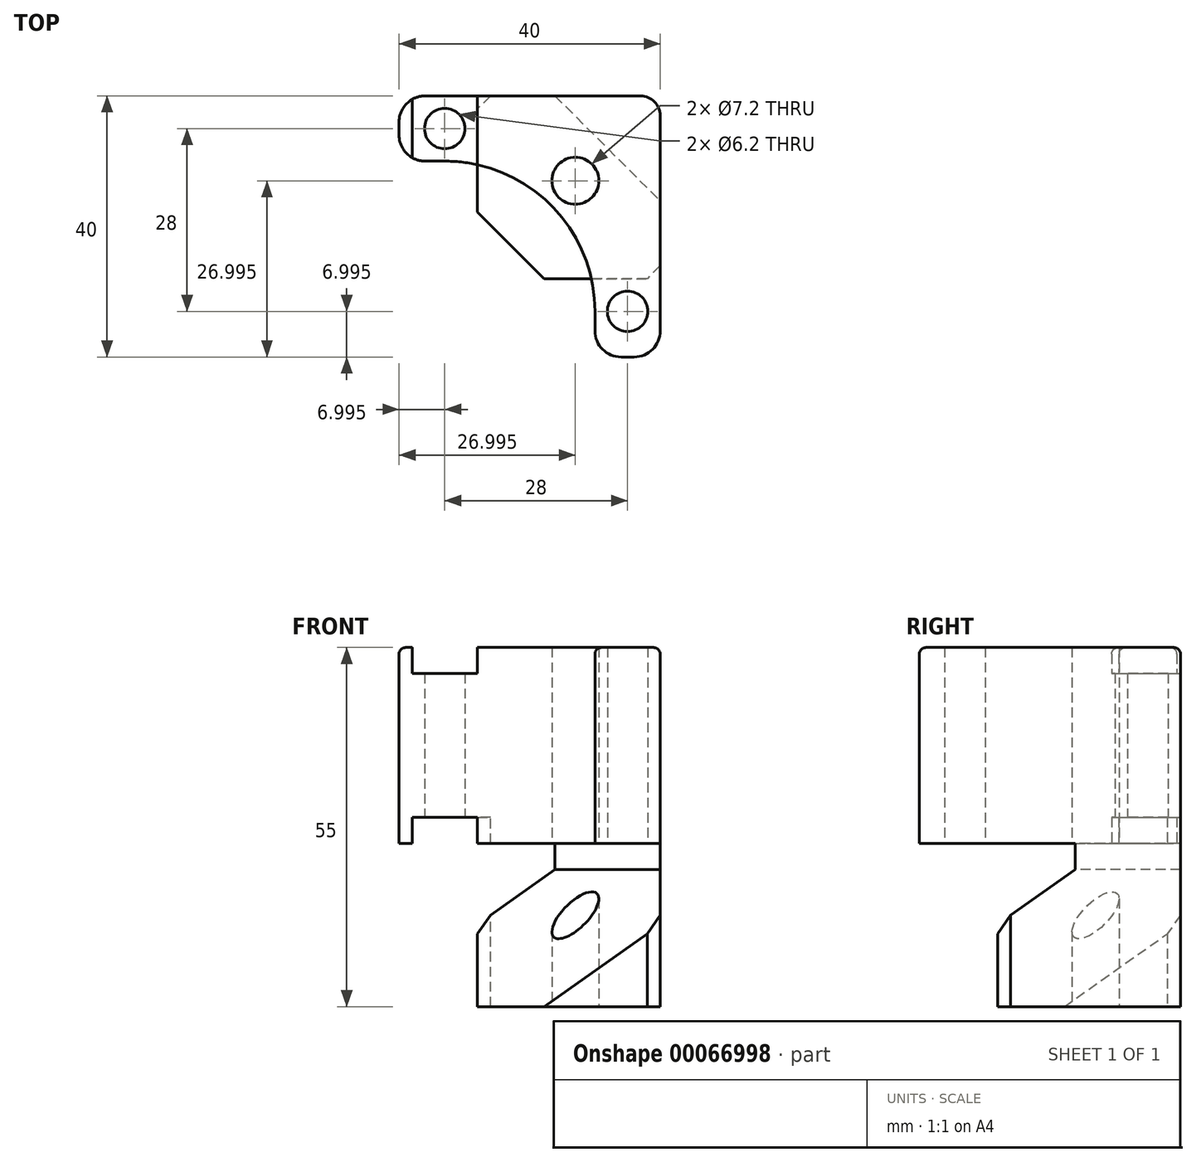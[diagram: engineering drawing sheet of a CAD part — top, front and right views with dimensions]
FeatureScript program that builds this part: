
annotation { "Feature Type Name" : "Feature", "Feature Type Description" : "" }
export const myFeature = defineFeature(function(context is Context, id is Id, definition is map)
    precondition{}
    {
        {
            var Q0;
            Q0=qCreatedBy(makeId("Top.planeOp"),FACE);
            var sketch = newSketch(context, id + "F0", { "sketchPlane" : qUnion([Q0])});
            skCircle(sketch, "E0", {"center": v(0, 0) * mm, "radius": 27.5 * mm, "construction": true});
            skLineSegment(sketch, "E1", {"start": v(-16.55, 19.45) * mm, "end": v(16.45, 19.45) * mm});
            skLineSegment(sketch, "E2", {"start": v(15.45, -20.55) * mm, "end": v(13.45, -20.55) * mm});
            skLineSegment(sketch, "E3", {"start": v(9.45, -16.55) * mm, "end": v(9.45, -13.55) * mm});
            skLineSegment(sketch, "E4", {"start": v(-13.55, 9.45) * mm, "end": v(-16.55, 9.45) * mm});
            skLineSegment(sketch, "E5", {"start": v(-20.55, 13.45) * mm, "end": v(-20.55, 15.45) * mm});
            skLineSegment(sketch, "E6", {"start": v(19.45, 16.45) * mm, "end": v(19.45, -16.55) * mm});
            skPoint(sketch, "E7.visualSharp", {"position": v(19.45, 19.45) * mm});
            skArc(sketch, "E7.filletArc", {"start": v(19.45, 16.45) * mm, "mid": v(18.57, 18.57) * mm, "end": v(16.45, 19.45) * mm});
            skPoint(sketch, "E8.visualSharp", {"position": v(-20.55, 19.45) * mm});
            skArc(sketch, "E8.filletArc", {"start": v(-16.55, 19.45) * mm, "mid": v(-19.38, 18.27) * mm, "end": v(-20.55, 15.45) * mm});
            skPoint(sketch, "E9.visualSharp", {"position": v(-20.55, 9.45) * mm});
            skArc(sketch, "E9.filletArc", {"start": v(-20.55, 13.45) * mm, "mid": v(-19.38, 10.62) * mm, "end": v(-16.55, 9.45) * mm});
            skPoint(sketch, "E10.visualSharp", {"position": v(9.45, -20.55) * mm});
            skArc(sketch, "E10.filletArc", {"start": v(9.45, -16.55) * mm, "mid": v(10.62, -19.38) * mm, "end": v(13.45, -20.55) * mm});
            skPoint(sketch, "E11.visualSharp", {"position": v(19.45, -20.55) * mm});
            skArc(sketch, "E11.filletArc", {"start": v(15.45, -20.55) * mm, "mid": v(18.27, -19.38) * mm, "end": v(19.45, -16.55) * mm});
            skLineSegment(sketch, "E12", {"start": v(0, 0) * mm, "end": v(19.45, 19.45) * mm, "construction": true});
            skPoint(sketch, "E13.visualSharp", {"position": v(9.45, 9.45) * mm});
            skArc(sketch, "E13.filletArc", {"start": v(9.45, -13.55) * mm, "mid": v(2.7, 2.7) * mm, "end": v(-13.55, 9.45) * mm});
            skCircle(sketch, "E14", {"center": v(6.45, 6.45) * mm, "radius": 3.6 * mm});
            skCircle(sketch, "E15", {"center": v(-13.55, 14.45) * mm, "radius": 3.1 * mm});
            skCircle(sketch, "E16", {"center": v(14.45, -13.55) * mm, "radius": 3.1 * mm});
            skLineSegment(sketch, "E17", {"start": v(-13.55, 14.45) * mm, "end": v(14.45, -13.55) * mm, "construction": true});
            skSolve(sketch);
        }
        {
            var Q0;
            Q0 = qSketchRegion(id + "F0", true);
            extrude(context, id + "F1", {"entities" : qUnion([Q0]), "depth" : 30 * mm});
        }
        {
            var Q0;
            Q0=makeQuery(id+"F1.opExtrude","SWEPT_FACE",FACE,{"disambiguationData":[OSD([sQuery(id+"F0.wireOp",EDGE,"E1")])]});
            var sketch = newSketch(context, id + "F2", { "sketchPlane" : qUnion([Q0])});
            skLineSegment(sketch, "E18.bottom", {"start": v(8.55, 30) * mm, "end": v(18.55, 30) * mm});
            skLineSegment(sketch, "E18.top", {"start": v(8.55, 26) * mm, "end": v(18.55, 26) * mm});
            skLineSegment(sketch, "E18.left", {"start": v(8.55, 30) * mm, "end": v(8.55, 26) * mm});
            skLineSegment(sketch, "E18.right", {"start": v(18.55, 30) * mm, "end": v(18.55, 26) * mm});
            skLineSegment(sketch, "E19.bottom", {"start": v(8.55, 0) * mm, "end": v(18.55, 0) * mm});
            skLineSegment(sketch, "E19.top", {"start": v(8.55, 4) * mm, "end": v(18.55, 4) * mm});
            skLineSegment(sketch, "E19.left", {"start": v(8.55, 0) * mm, "end": v(8.55, 4) * mm});
            skLineSegment(sketch, "E19.right", {"start": v(18.55, 0) * mm, "end": v(18.55, 4) * mm});
            skSolve(sketch);
        }
        {
            var Q0;
            Q0 = qSketchRegion(id + "F2", true);
            extrude(context, id + "F3", {"entities" : qUnion([Q0]), "operationType" : NewBodyOperationType.REMOVE, "endBound" : BoundingType.THROUGH_ALL, "oppositeDirection" : true, "depth" : 25 * mm});
        }
        {
            var Q0;
            Q0=makeQuery(id+"F1.opExtrude","CAP_EDGE",EDGE,{"disambiguationData":[OSD([sQuery(id+"F0.wireOp",EDGE,"E13.filletArc")])],"isStart":false});
            var Q1;
            Q1=makeQuery(id+"F1.opExtrude","CAP_EDGE",EDGE,{"disambiguationData":[OSD([sQuery(id+"F0.wireOp",EDGE,"E5")])],"isStart":false});
            var Q2;
            Q2=makeQuery(id+"F3.boolean.opBoolean","COPY",EDGE,{"derivedFrom":makeQuery(id+"F3.opExtrude","SWEPT_EDGE",EDGE,{"disambiguationData":[OSD([sQuery(id+"F0.wireOp",EDGE,"E1"),sQuery(id+"F2.wireOp",EDGE,"E18.bottom"),sQuery(id+"F2.wireOp",EDGE,"E18.left")])]})});
            fillet(context, id + "F4", {"entities" : qUnion([Q0, Q1, Q2]), "radius" : 1 * mm, "tangentPropagation" : true, "allowEdgeOverflow" : false});
        }
        {
            var Q0;
            {var subQ0=sQuery(id+"F0.wireOp",EDGE,"E13.filletArc");var subQ1=sQuery(id+"F0.wireOp",EDGE,"E11.filletArc");var subQ2=sQuery(id+"F0.wireOp",EDGE,"E10.filletArc");var subQ3=sQuery(id+"F0.wireOp",EDGE,"E7.filletArc");var subQ4=sQuery(id+"F0.wireOp",EDGE,"E1");var subQ5=sQuery(id+"F0.wireOp",EDGE,"E2");var subQ6=sQuery(id+"F0.wireOp",EDGE,"E16");var subQ7=sQuery(id+"F0.wireOp",EDGE,"E3");var subQ8=sQuery(id+"F0.wireOp",EDGE,"E14");var subQ9=sQuery(id+"F0.wireOp",EDGE,"E6");Q0=makeQuery(id+"F3.boolean.opBoolean","SPLIT",FACE,{"disambiguationData":[TD([makeQuery(id+"F1.opExtrude","SWEPT_FACE",FACE,{"disambiguationData":[OSD([subQ4])]})])],"derivedFrom":makeQuery(id+"F1.opExtrude","CAP_FACE",FACE,{"disambiguationData":[OSD([subQ4,subQ5,subQ7,sQuery(id+"F0.wireOp",EDGE,"E4"),sQuery(id+"F0.wireOp",EDGE,"E5"),subQ9,subQ3,sQuery(id+"F0.wireOp",EDGE,"E8.filletArc"),sQuery(id+"F0.wireOp",EDGE,"E9.filletArc"),subQ2,subQ1,subQ0,subQ8,sQuery(id+"F0.wireOp",EDGE,"E15"),subQ6])],"isStart":true})});}
            var sketch = newSketch(context, id + "F5", { "sketchPlane" : qUnion([Q0])});
            skLineSegment(sketch, "E20", {"start": v(-8.55, -19.45) * mm, "end": v(16.45, -19.45) * mm});
            skPoint(sketch, "E20.endSnap0", {"position": v(18.57, -18.57) * mm});
            skLineSegment(sketch, "E21", {"start": v(19.45, -16.45) * mm, "end": v(19.45, 8.55) * mm});
            skLineSegment(sketch, "E22", {"start": v(19.45, 8.55) * mm, "end": v(-8.55, 8.55) * mm});
            skLineSegment(sketch, "E23", {"start": v(-8.55, 8.55) * mm, "end": v(-8.55, -19.45) * mm});
            skPoint(sketch, "E24.visualSharp", {"position": v(19.45, -19.45) * mm});
            skArc(sketch, "E24.filletArc", {"start": v(16.45, -19.45) * mm, "mid": v(18.57, -18.57) * mm, "end": v(19.45, -16.45) * mm});
            skCircle(sketch, "E25", {"center": v(6.45, -6.45) * mm, "radius": 3.6 * mm});
            skSolve(sketch);
        }
        {
            var Q0;
            Q0 = qSketchRegion(id + "F5", true);
            extrude(context, id + "F6", {"entities" : qUnion([Q0]), "operationType" : NewBodyOperationType.ADD, "depth" : 25 * mm});
        }
        {
            var Q0;
            Q0=makeQuery(id+"F6.opExtrude","SWEPT_EDGE",EDGE,{"disambiguationData":[OSD([sQuery(id+"F0.wireOp",EDGE,"E6"),sQuery(id+"F5.wireOp",EDGE,"E21"),sQuery(id+"F5.wireOp",EDGE,"E22")])]});
            var Q1;
            Q1=makeQuery(id+"F6.boolean.opBoolean","MERGE",EDGE,{"derivedFrom":[makeQuery(id+"F3.boolean.opBoolean","COPY",EDGE,{"derivedFrom":makeQuery(id+"F3.opExtrude","CAP_EDGE",EDGE,{"disambiguationData":[OSD([sQuery(id+"F2.wireOp",EDGE,"E19.left")])],"isStart":true})}),makeQuery(id+"F6.opExtrude","SWEPT_EDGE",EDGE,{"disambiguationData":[OSD([sQuery(id+"F5.wireOp",EDGE,"E20"),sQuery(id+"F5.wireOp",EDGE,"E23")])]})]});
            chamfer(context, id + "F7", {"entities" : qUnion([Q0, Q1]), "width" : 2 * mm, "tangentPropagation" : true});
        }
        {
            var Q0;
            Q0=makeQuery(id+"F7.opChamfer","BLEND_FACE",FACE,{"disambiguationData":[OSD([sQuery(id+"F0.wireOp",EDGE,"E6"),sQuery(id+"F5.wireOp",EDGE,"E21"),sQuery(id+"F5.wireOp",EDGE,"E22")])]});
            var sketch = newSketch(context, id + "F8", { "sketchPlane" : qUnion([Q0])});
            skLineSegment(sketch, "E26", {"start": v(16.12, 0) * mm, "end": v(-28.88, 0) * mm});
            skLineSegment(sketch, "E27", {"start": v(-28.88, 0) * mm, "end": v(-28.88, -49) * mm});
            skLineSegment(sketch, "E28", {"start": v(16.12, 0) * mm, "end": v(16.12, -4) * mm});
            skLineSegment(sketch, "E29", {"start": v(16.12, -4) * mm, "end": v(-28.88, -49) * mm});
            skSolve(sketch);
        }
        {
            var Q0;
            Q0 = qSketchRegion(id + "F8", true);
            extrude(context, id + "F9", {"entities" : qUnion([Q0]), "operationType" : NewBodyOperationType.REMOVE, "endBound" : BoundingType.THROUGH_ALL, "oppositeDirection" : true, "depth" : 25 * mm});
        }
    });
